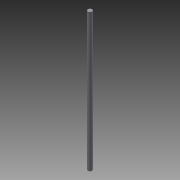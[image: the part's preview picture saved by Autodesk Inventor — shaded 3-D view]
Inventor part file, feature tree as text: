
AUTODESK INVENTOR PART (.ipt)
format: ipt  version: 2015 SP1 (Build 190203100, 203)  size: 71,680 bytes
history: native  units: mm
features: other x3, extrude x1, sketch x1
ambient origin geometry x8: Origin, YZ Plane, XZ Plane, XY Plane, X Axis, Y Axis, Z Axis, Center Point
bodies: Solid1 (feature_tree)
feature tree (5):
  other  "Table"
  other  "Shaft 12 400"
  other  "Shaft 12 450"
  extrude  "Extrusion1"  TaperAngle=0.0deg  [1 undecoded]
  sketch  "Sketch1"  dims[d0=12.0mm d2=0.0mm]
note: 1 required parameter value undecoded (feature->parameter linkage not recoverable at this tier; creation-order binding heuristic only, values carry confidence <= 0.55)
